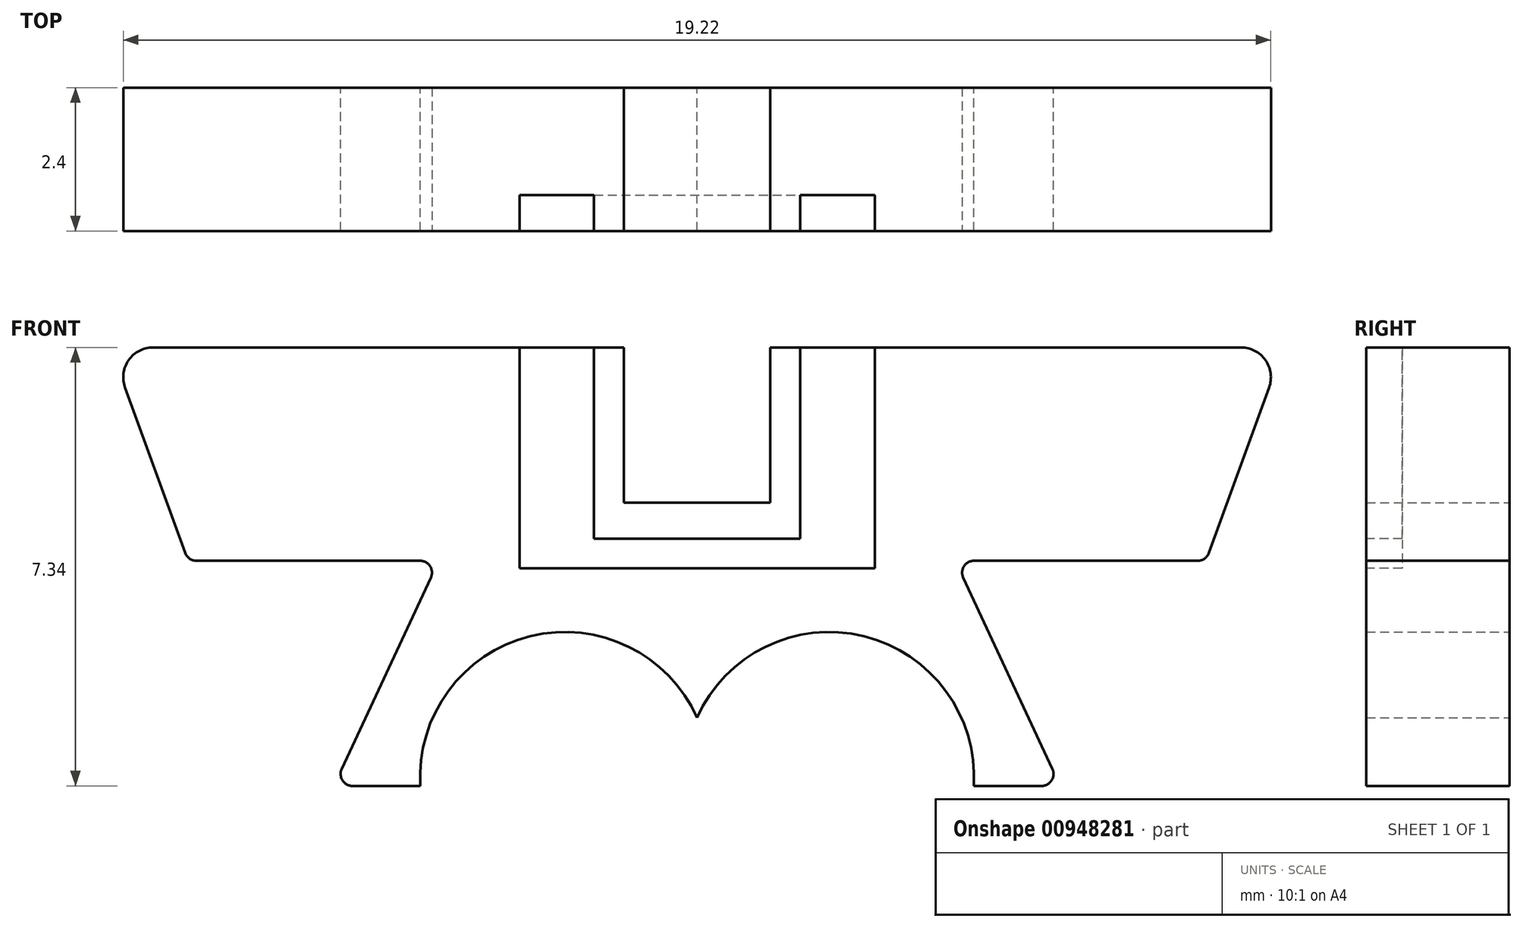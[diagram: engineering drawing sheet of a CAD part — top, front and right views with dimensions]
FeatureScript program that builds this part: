
annotation { "Feature Type Name" : "Feature", "Feature Type Description" : "" }
export const myFeature = defineFeature(function(context is Context, id is Id, definition is map)
    precondition{}
    {
        {
            var Q0;
            Q0=qCreatedBy(makeId("Front.planeOp"),FACE);
            var sketch = newSketch(context, id + "F0", { "sketchPlane" : qUnion([Q0])});
            skLineSegment(sketch, "E0", {"start": v(0, 0) * mm, "end": v(1.23, 0) * mm});
            skLineSegment(sketch, "E1", {"start": v(1.23, 0) * mm, "end": v(1.23, 2.6) * mm});
            skLineSegment(sketch, "E2", {"start": v(1.23, 2.6) * mm, "end": v(9.83, 2.6) * mm});
            skLineSegment(sketch, "E3", {"start": v(9.83, 2.6) * mm, "end": v(8.53, -0.97) * mm});
            skLineSegment(sketch, "E4", {"start": v(8.53, -0.97) * mm, "end": v(4.33, -0.97) * mm});
            skLineSegment(sketch, "E5", {"start": v(4.33, -0.97) * mm, "end": v(6.08, -4.74) * mm});
            skLineSegment(sketch, "E6", {"start": v(6.08, -4.74) * mm, "end": v(4.63, -4.74) * mm});
            skArc(sketch, "E7", {"start": v(4.63, -4.74) * mm, "mid": v(2.8, -2.24) * mm, "end": v(0, -3.6) * mm});
            skLineSegment(sketch, "E8", {"start": v(0, -3.6) * mm, "end": v(0, 0) * mm});
            skSolve(sketch);
        }
        {
            var Q0;
            Q0=makeQuery(id+"F0.imprint","IMPRINT",FACE,{"disambiguationData":[TD([[makeQuery(id+"F0.imprint","IMPRINT",EDGE,{"derivedFrom":sQuery(id+"F0.wireOp",EDGE,"E0")}),-1.0]])]});
            extrude(context, id + "F1", {"entities" : qUnion([Q0]), "depth" : 2.4 * mm, "offsetDistance" : 25 * mm});
        }
        {
            var Q0;
            Q0=makeQuery(id+"F1.opExtrude","SWEPT_BODY",BODY,{"disambiguationData":[OSD([sQuery(id+"F0.wireOp",EDGE,"E0"),sQuery(id+"F0.wireOp",EDGE,"E1"),sQuery(id+"F0.wireOp",EDGE,"E2"),sQuery(id+"F0.wireOp",EDGE,"E3"),sQuery(id+"F0.wireOp",EDGE,"E4"),sQuery(id+"F0.wireOp",EDGE,"E5"),sQuery(id+"F0.wireOp",EDGE,"E6"),sQuery(id+"F0.wireOp",EDGE,"E7"),sQuery(id+"F0.wireOp",EDGE,"E8")])]});
            var Q1;
            Q1=makeQuery(id+"F1.opExtrude","SWEPT_FACE",FACE,{"disambiguationData":[OSD([sQuery(id+"F0.wireOp",EDGE,"E8")])]});
            mirror(context, id + "F2", {"operationType" : NewBodyOperationType.ADD, "entities" : qUnion([Q0]), "mirrorPlane" : qUnion([Q1])});
        }
        {
            var Q0;
            Q0=makeQuery(id+"F2.opPattern","COPY",EDGE,{"derivedFrom":makeQuery(id+"F1.opExtrude","SWEPT_EDGE",EDGE,{"disambiguationData":[OSD([sQuery(id+"F0.wireOp",EDGE,"E2"),sQuery(id+"F0.wireOp",EDGE,"E3")])]}),"instanceName":"1"});
            var Q1;
            Q1=makeQuery(id+"F1.opExtrude","SWEPT_EDGE",EDGE,{"disambiguationData":[OSD([sQuery(id+"F0.wireOp",EDGE,"E2"),sQuery(id+"F0.wireOp",EDGE,"E3")])]});
            fillet(context, id + "F3", {"entities" : qUnion([Q0, Q1]), "radius" : 0.5 * mm, "tangentPropagation" : true, "allowEdgeOverflow" : false});
        }
        {
            var Q0;
            Q0=makeQuery(id+"F2.opPattern","COPY",EDGE,{"derivedFrom":makeQuery(id+"F1.opExtrude","SWEPT_EDGE",EDGE,{"disambiguationData":[OSD([sQuery(id+"F0.wireOp",EDGE,"E3"),sQuery(id+"F0.wireOp",EDGE,"E4")])]}),"instanceName":"1"});
            var Q1;
            Q1=makeQuery(id+"F1.opExtrude","SWEPT_EDGE",EDGE,{"disambiguationData":[OSD([sQuery(id+"F0.wireOp",EDGE,"E3"),sQuery(id+"F0.wireOp",EDGE,"E4")])]});
            fillet(context, id + "F4", {"entities" : qUnion([Q0, Q1]), "radius" : 0.2 * mm, "tangentPropagation" : true, "allowEdgeOverflow" : false});
        }
        {
            var Q0;
            Q0=makeQuery(id+"F2.opPattern","COPY",EDGE,{"derivedFrom":makeQuery(id+"F1.opExtrude","SWEPT_EDGE",EDGE,{"disambiguationData":[OSD([sQuery(id+"F0.wireOp",EDGE,"E5"),sQuery(id+"F0.wireOp",EDGE,"E6")])]}),"instanceName":"1"});
            var Q1;
            Q1=makeQuery(id+"F1.opExtrude","SWEPT_EDGE",EDGE,{"disambiguationData":[OSD([sQuery(id+"F0.wireOp",EDGE,"E5"),sQuery(id+"F0.wireOp",EDGE,"E6")])]});
            fillet(context, id + "F5", {"entities" : qUnion([Q0, Q1]), "radius" : 0.2 * mm, "tangentPropagation" : true, "allowEdgeOverflow" : false});
        }
        {
            var Q0;
            Q0=makeQuery(id+"F2.opPattern","COPY",EDGE,{"derivedFrom":makeQuery(id+"F1.opExtrude","SWEPT_EDGE",EDGE,{"disambiguationData":[OSD([sQuery(id+"F0.wireOp",EDGE,"E4"),sQuery(id+"F0.wireOp",EDGE,"E5")])]}),"instanceName":"1"});
            var Q1;
            Q1=makeQuery(id+"F1.opExtrude","SWEPT_EDGE",EDGE,{"disambiguationData":[OSD([sQuery(id+"F0.wireOp",EDGE,"E4"),sQuery(id+"F0.wireOp",EDGE,"E5")])]});
            fillet(context, id + "F6", {"entities" : qUnion([Q0, Q1]), "radius" : 0.2 * mm, "tangentPropagation" : true, "allowEdgeOverflow" : false});
        }
        {
            var Q0;
            {var subQ0=makeQuery(id+"F1.opExtrude","CAP_FACE",FACE,{"disambiguationData":[OSD([sQuery(id+"F0.wireOp",EDGE,"E0"),sQuery(id+"F0.wireOp",EDGE,"E1"),sQuery(id+"F0.wireOp",EDGE,"E2"),sQuery(id+"F0.wireOp",EDGE,"E3"),sQuery(id+"F0.wireOp",EDGE,"E4"),sQuery(id+"F0.wireOp",EDGE,"E5"),sQuery(id+"F0.wireOp",EDGE,"E6"),sQuery(id+"F0.wireOp",EDGE,"E7"),sQuery(id+"F0.wireOp",EDGE,"E8")])],"isStart":false});Q0=makeQuery(id+"F2.boolean.opBoolean","MERGE",FACE,{"derivedFrom":[subQ0,makeQuery(id+"F2.opPattern","COPY",FACE,{"derivedFrom":subQ0,"instanceName":"1"})]});}
            var sketch = newSketch(context, id + "F7", { "sketchPlane" : qUnion([Q0])});
            skLineSegment(sketch, "E9.0", {"start": v(-1.72, -0.6) * mm, "end": v(-1.73, 2.6) * mm});
            skLineSegment(sketch, "E10.0", {"start": v(-1.72, -0.6) * mm, "end": v(1.73, -0.6) * mm});
            skLineSegment(sketch, "E11.0", {"start": v(1.73, -0.6) * mm, "end": v(1.73, 2.6) * mm});
            skLineSegment(sketch, "E12", {"start": v(-2.98, 2.6) * mm, "end": v(-2.97, -1.1) * mm});
            skLineSegment(sketch, "E13", {"start": v(-2.97, -1.1) * mm, "end": v(2.98, -1.1) * mm});
            skLineSegment(sketch, "E14", {"start": v(2.98, -1.1) * mm, "end": v(2.98, 2.6) * mm});
            skLineSegment(sketch, "E15", {"start": v(-2.98, 2.6) * mm, "end": v(-1.73, 2.6) * mm});
            skLineSegment(sketch, "E16", {"start": v(1.73, 2.6) * mm, "end": v(2.98, 2.6) * mm});
            skLineSegment(sketch, "E17.0", {"start": v(-1.23, 0) * mm, "end": v(-1.23, 2.6) * mm, "construction": true});
            skLineSegment(sketch, "E18.0", {"start": v(-1.22, 0) * mm, "end": v(1.23, 0) * mm, "construction": true});
            skLineSegment(sketch, "E19.0", {"start": v(1.23, 0) * mm, "end": v(1.23, 2.6) * mm, "construction": true});
            skSolve(sketch);
        }
        {
            var Q0;
            Q0=makeQuery(id+"F7.imprint","IMPRINT",FACE,{"disambiguationData":[TD([[makeQuery(id+"F7.imprint","IMPRINT",EDGE,{"derivedFrom":sQuery(id+"F7.wireOp",EDGE,"E9.0")}),1.0]])]});
            extrude(context, id + "F8", {"entities" : qUnion([Q0]), "operationType" : NewBodyOperationType.REMOVE, "oppositeDirection" : true, "depth" : .6 * mm, "offsetDistance" : 25 * mm});
        }
    });
